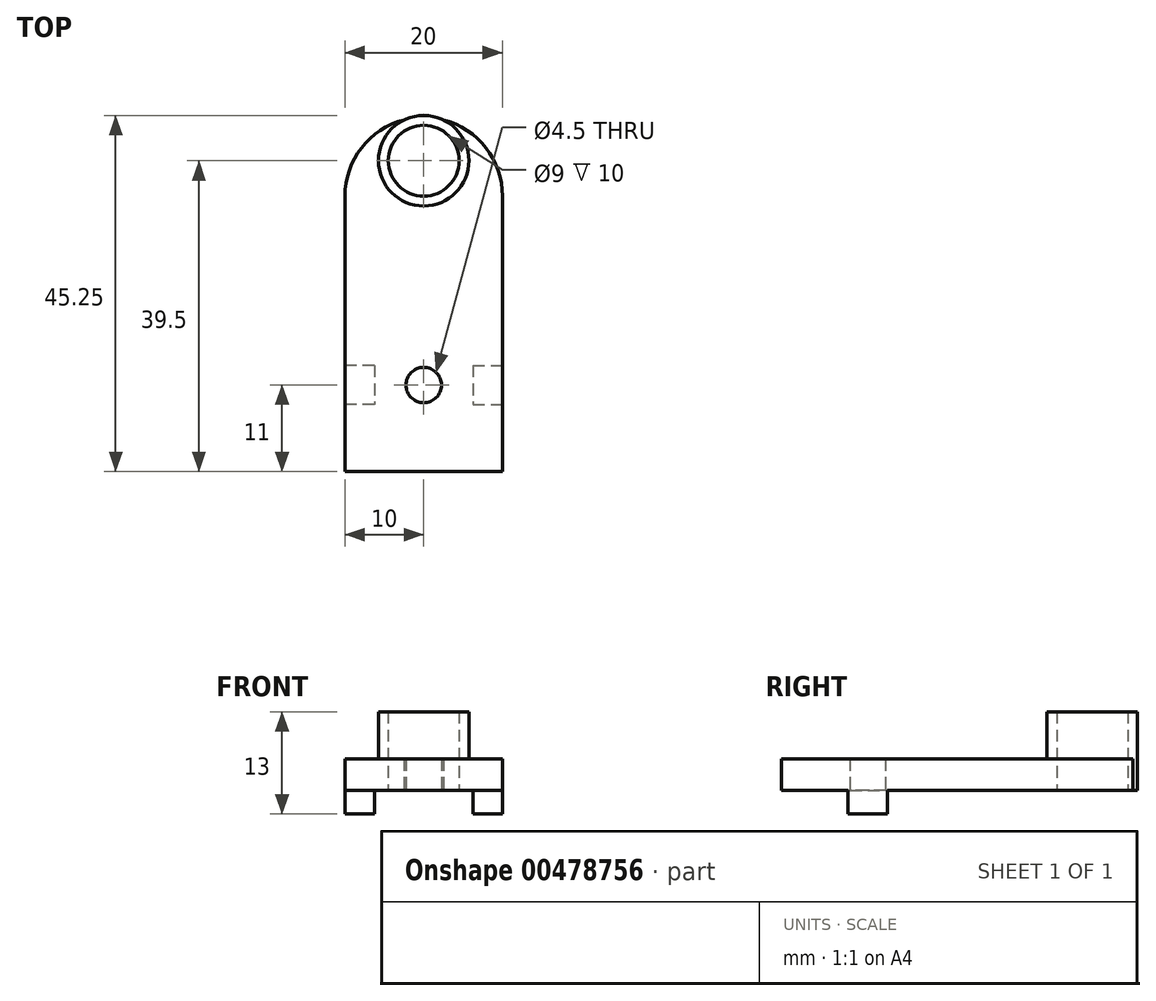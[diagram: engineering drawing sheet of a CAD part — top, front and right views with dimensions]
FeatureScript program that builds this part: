
annotation { "Feature Type Name" : "Feature", "Feature Type Description" : "" }
export const myFeature = defineFeature(function(context is Context, id is Id, definition is map)
    precondition{}
    {
        {
            var Q0;
            Q0=qCreatedBy(makeId("Top.planeOp"),FACE);
            var sketch = newSketch(context, id + "F0", { "sketchPlane" : qUnion([Q0])});
            skLineSegment(sketch, "E0", {"start": v(-10, 0) * mm, "end": v(10, 0) * mm});
            skLineSegment(sketch, "E1", {"start": v(10, 0) * mm, "end": v(10, 35) * mm});
            skLineSegment(sketch, "E2", {"start": v(-10, 0) * mm, "end": v(-10, 35) * mm});
            skLineSegment(sketch, "E3", {"start": v(10, 35) * mm, "end": v(-10, 35) * mm, "construction": true});
            skCircle(sketch, "E4", {"center": v(0, 11) * mm, "radius": 2.25 * mm});
            skCircle(sketch, "E5", {"center": v(0, 39.5) * mm, "radius": 4.5 * mm});
            skArc(sketch, "E6", {"start": v(10, 35) * mm, "mid": v(0, 45) * mm, "end": v(-10, 35) * mm});
            skSolve(sketch);
        }
        {
            var Q0;
            Q0=makeQuery(id+"F0.imprint","IMPRINT",FACE,{"disambiguationData":[TD([[makeQuery(id+"F0.imprint","IMPRINT",EDGE,{"derivedFrom":sQuery(id+"F0.wireOp",EDGE,"E0")}),1.0]])]});
            extrude(context, id + "F1", {"entities" : qUnion([Q0]), "depth" : 4 * mm});
        }
        {
            var Q0;
            Q0=qCreatedBy(makeId("Top.planeOp"),FACE);
            var sketch = newSketch(context, id + "F2", { "sketchPlane" : qUnion([Q0])});
            skLineSegment(sketch, "E7.bottom", {"start": v(-6.25, 13.5) * mm, "end": v(-10, 13.5) * mm});
            skLineSegment(sketch, "E7.top", {"start": v(-6.25, 8.5) * mm, "end": v(-10, 8.5) * mm});
            skLineSegment(sketch, "E7.left", {"start": v(-6.25, 13.5) * mm, "end": v(-6.25, 8.5) * mm});
            skLineSegment(sketch, "E7.right", {"start": v(-10, 13.5) * mm, "end": v(-10, 8.5) * mm});
            skLineSegment(sketch, "E8.bottom", {"start": v(6.25, 13.5) * mm, "end": v(10, 13.5) * mm});
            skLineSegment(sketch, "E8.top", {"start": v(6.25, 8.5) * mm, "end": v(10, 8.5) * mm});
            skLineSegment(sketch, "E8.left", {"start": v(6.25, 13.5) * mm, "end": v(6.25, 8.5) * mm});
            skLineSegment(sketch, "E8.right", {"start": v(10, 13.5) * mm, "end": v(10, 8.5) * mm});
            skSolve(sketch);
        }
        {
            var Q0;
            Q0 = qSketchRegion(id + "F2", true);
            extrude(context, id + "F3", {"entities" : qUnion([Q0]), "operationType" : NewBodyOperationType.ADD, "oppositeDirection" : true, "depth" : 3 * mm});
        }
        {
            var Q0;
            Q0=makeQuery(id+"F1.opExtrude","CAP_FACE",FACE,{"disambiguationData":[OSD([sQuery(id+"F0.wireOp",EDGE,"E0"),sQuery(id+"F0.wireOp",EDGE,"E1"),sQuery(id+"F0.wireOp",EDGE,"E2"),sQuery(id+"F0.wireOp",EDGE,"E4"),sQuery(id+"F0.wireOp",EDGE,"E5"),sQuery(id+"F0.wireOp",EDGE,"E6")])],"isStart":true});
            var sketch = newSketch(context, id + "F4", { "sketchPlane" : qUnion([Q0])});
            skCircle(sketch, "E9", {"center": v(0, -39.5) * mm, "radius": 5.75 * mm});
            skSolve(sketch);
        }
        {
            var Q0;
            {var subQ0=sQuery(id+"F4.wireOp",EDGE,"E9");var subQ1=makeQuery(id+"F1.opExtrude","CAP_EDGE",EDGE,{"disambiguationData":[OSD([sQuery(id+"F0.wireOp",EDGE,"E6")])],"isStart":true});var subQ2=makeQuery(id+"F4.imprint","INTERSECT",VERTEX,{"disambiguationData":[OD(0.0)],"derivedFrom":[subQ1,subQ0]});Q0=makeQuery(id+"F4.imprint","IMPRINT",FACE,{"disambiguationData":[TD([[makeQuery(id+"F4.imprint","IMPRINT",EDGE,{"disambiguationData":[TD([[subQ2,1.0]])],"derivedFrom":subQ0}),1.0]])]});}
            var Q1;
            Q1=makeQuery(id+"F4.imprint","IMPRINT",FACE,{"disambiguationData":[TD([[makeQuery(id+"F4.imprint","IMPRINT",EDGE,{"derivedFrom":makeQuery(id+"F1.opExtrude","CAP_EDGE",EDGE,{"disambiguationData":[OSD([sQuery(id+"F0.wireOp",EDGE,"E5")])],"isStart":true})}),1.0]])]});
            extrude(context, id + "F5", {"entities" : qUnion([Q0, Q1]), "operationType" : NewBodyOperationType.ADD, "oppositeDirection" : true, "depth" : 10 * mm});
        }
    });
